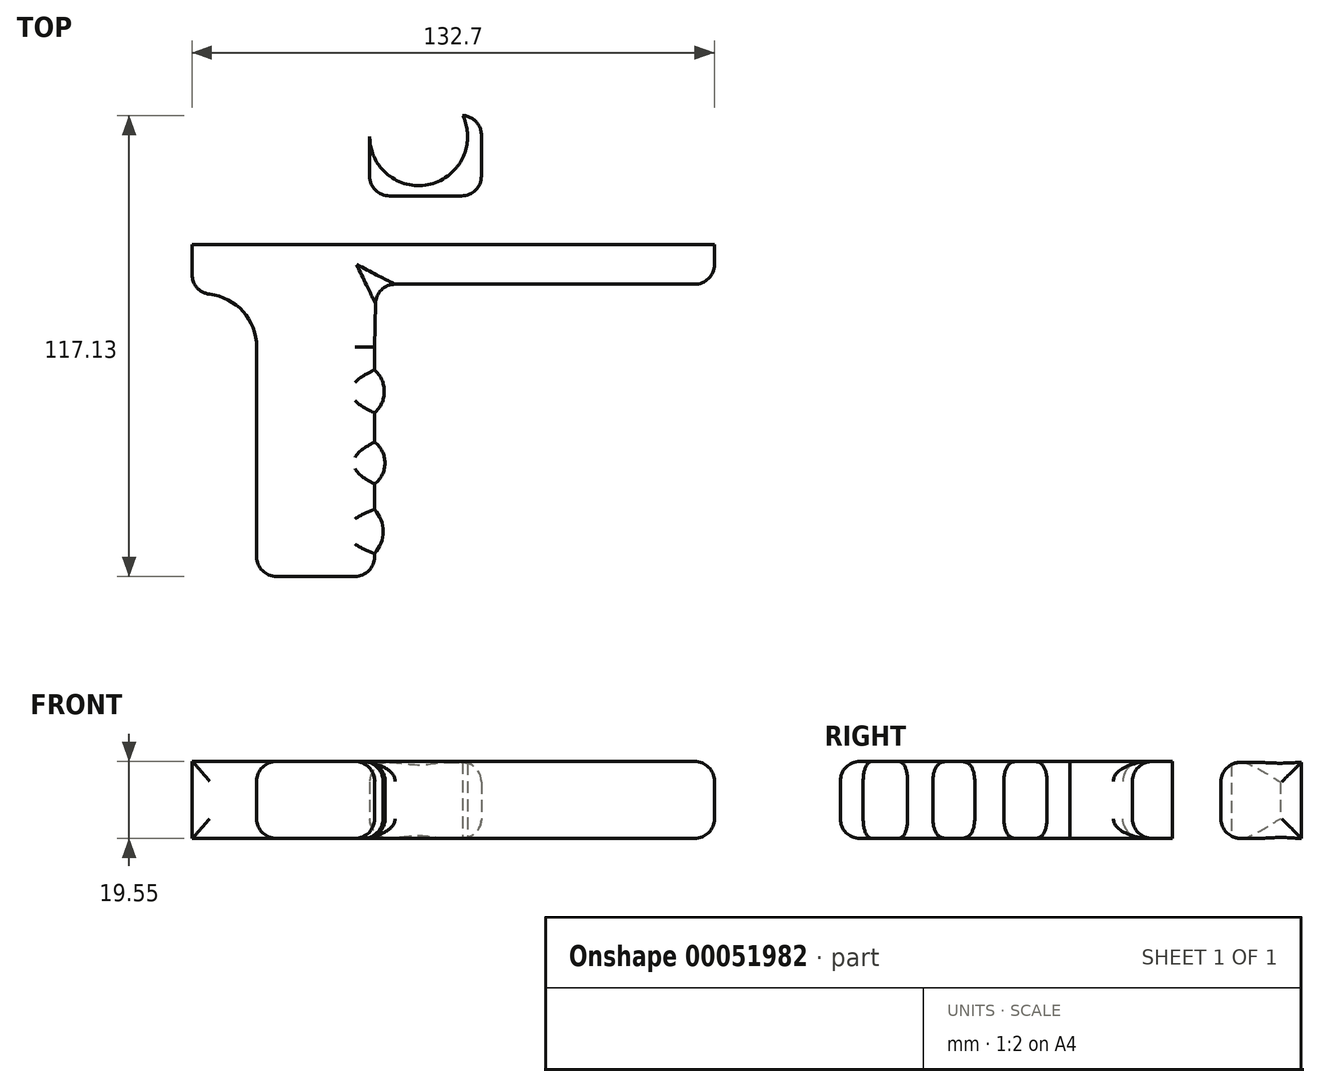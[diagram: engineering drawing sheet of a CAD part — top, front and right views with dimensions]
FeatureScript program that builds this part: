
annotation { "Feature Type Name" : "Feature", "Feature Type Description" : "" }
export const myFeature = defineFeature(function(context is Context, id is Id, definition is map)
    precondition{}
    {
        {
            var Q0;
            Q0=qCreatedBy(makeId("Top.planeOp"),FACE);
            var sketch = newSketch(context, id + "F0", { "sketchPlane" : qUnion([Q0])});
            skLineSegment(sketch, "E0.bottom", {"start": v(-44.45, -15.94) * mm, "end": v(-14.5, -15.94) * mm});
            skLineSegment(sketch, "E0.top", {"start": v(-44.45, -74.24) * mm, "end": v(-14.5, -74.24) * mm});
            skLineSegment(sketch, "E0.left", {"start": v(-44.45, -15.94) * mm, "end": v(-44.45, -74.24) * mm});
            skLineSegment(sketch, "E0.right", {"start": v(-14.5, -15.94) * mm, "end": v(-14.5, -74.24) * mm});
            skArc(sketch, "E1", {"start": v(-44.45, -15.94) * mm, "mid": v(-49.5, -5.4) * mm, "end": v(-60.87, -2.74) * mm});
            skLineSegment(sketch, "E2", {"start": v(-60.87, -2.74) * mm, "end": v(-60.87, 10.15) * mm});
            skLineSegment(sketch, "E3", {"start": v(-60.87, 10.15) * mm, "end": v(71.83, 10.15) * mm});
            skLineSegment(sketch, "E4", {"start": v(71.83, 10.15) * mm, "end": v(71.83, 0) * mm});
            skLineSegment(sketch, "E5", {"start": v(71.83, 0) * mm, "end": v(-6.76, 0) * mm});
            skLineSegment(sketch, "E6", {"start": v(-6.76, 0) * mm, "end": v(-14.17, 0) * mm});
            skLineSegment(sketch, "E7", {"start": v(-14.17, 0) * mm, "end": v(-14.5, -15.94) * mm});
            skArc(sketch, "E8", {"start": v(-14.5, -32.7) * mm, "mid": v(-12.02, -27.22) * mm, "end": v(-14.5, -21.74) * mm});
            skArc(sketch, "E9", {"start": v(-14.5, -50.73) * mm, "mid": v(-11.85, -45.41) * mm, "end": v(-14.5, -40.1) * mm});
            skArc(sketch, "E10", {"start": v(-14.5, -68.44) * mm, "mid": v(-12.36, -62.8) * mm, "end": v(-14.5, -57.17) * mm});
            skArc(sketch, "E11", {"start": v(-14.5, -15.94) * mm, "mid": v(6.33, -18.77) * mm, "end": v(15.78, 0) * mm});
            skArc(sketch, "E12", {"start": v(-6.76, 0) * mm, "mid": v(-7.48, -9.58) * mm, "end": v(0, -15.62) * mm});
            skArc(sketch, "E13", {"start": v(-4, 0) * mm, "mid": v(-4.47, -8.44) * mm, "end": v(0, -15.62) * mm});
            skSolve(sketch);
        }
        {
            var Q0;
            {var subQ0=sQuery(id+"F0.wireOp",EDGE,"E8");Q0=makeQuery(id+"F0.imprint","IMPRINT",FACE,{"disambiguationData":[TD([[makeQuery(id+"F0.imprint","IMPRINT",EDGE,{"derivedFrom":subQ0}),1.0]])]});}
            var Q1;
            {var subQ0=sQuery(id+"F0.wireOp",EDGE,"E9");Q1=makeQuery(id+"F0.imprint","IMPRINT",FACE,{"disambiguationData":[TD([[makeQuery(id+"F0.imprint","IMPRINT",EDGE,{"derivedFrom":subQ0}),1.0]])]});}
            var Q2;
            {var subQ0=sQuery(id+"F0.wireOp",EDGE,"E10");Q2=makeQuery(id+"F0.imprint","IMPRINT",FACE,{"disambiguationData":[TD([[makeQuery(id+"F0.imprint","IMPRINT",EDGE,{"derivedFrom":subQ0}),1.0]])]});}
            var Q3;
            Q3=makeQuery(id+"F0.imprint","IMPRINT",FACE,{"disambiguationData":[TD([[makeQuery(id+"F0.imprint","IMPRINT",EDGE,{"derivedFrom":sQuery(id+"F0.wireOp",EDGE,"E0.bottom")}),1.0]])]});
            var Q4;
            {var subQ1=sQuery(id+"F0.wireOp",EDGE,"E0.bottom");Q4=makeQuery(id+"F0.imprint","IMPRINT",FACE,{"disambiguationData":[TD([[makeQuery(id+"F0.imprint","IMPRINT",EDGE,{"derivedFrom":subQ1}),-1.0]])]});}
            extrude(context, id + "F1", {"entities" : qUnion([Q0, Q1, Q2, Q3, Q4]), "depth" : 19.55 * mm});
        }
        {
            var Q0;
            Q0=makeQuery(id+"F1.opExtrude","SWEPT_EDGE",EDGE,{"disambiguationData":[OSD([sQuery(id+"F0.wireOp",EDGE,"E4"),sQuery(id+"F0.wireOp",EDGE,"E5")])]});
            var Q1;
            Q1=makeQuery(id+"F1.opExtrude","SWEPT_EDGE",EDGE,{"disambiguationData":[OSD([sQuery(id+"F0.wireOp",EDGE,"E1"),sQuery(id+"F0.wireOp",EDGE,"E2")])]});
            var Q2;
            Q2=makeQuery(id+"F1.opExtrude","SWEPT_EDGE",EDGE,{"disambiguationData":[OSD([sQuery(id+"F0.wireOp",EDGE,"E0.top"),sQuery(id+"F0.wireOp",EDGE,"E0.left")])]});
            var Q3;
            Q3=makeQuery(id+"F1.opExtrude","SWEPT_EDGE",EDGE,{"disambiguationData":[OSD([sQuery(id+"F0.wireOp",EDGE,"E0.top"),sQuery(id+"F0.wireOp",EDGE,"E0.right")])]});
            var Q4;
            Q4=makeQuery(id+"F1.opExtrude","CAP_EDGE",EDGE,{"disambiguationData":[OSD([sQuery(id+"F0.wireOp",EDGE,"E0.left")])],"isStart":false});
            var Q5;
            Q5=makeQuery(id+"F1.opExtrude","CAP_EDGE",EDGE,{"disambiguationData":[OSD([sQuery(id+"F0.wireOp",EDGE,"E0.left")])],"isStart":true});
            var Q6;
            Q6=makeQuery(id+"F1.opExtrude","CAP_EDGE",EDGE,{"disambiguationData":[OSD([sQuery(id+"F0.wireOp",EDGE,"E5"),sQuery(id+"F0.wireOp",EDGE,"E6")])],"isStart":false});
            var Q7;
            Q7=makeQuery(id+"F1.opExtrude","CAP_EDGE",EDGE,{"disambiguationData":[OSD([sQuery(id+"F0.wireOp",EDGE,"E5"),sQuery(id+"F0.wireOp",EDGE,"E6")])],"isStart":true});
            var Q8;
            Q8=makeQuery(id+"F1.opExtrude","CAP_EDGE",EDGE,{"disambiguationData":[OSD([sQuery(id+"F0.wireOp",EDGE,"E7")])],"isStart":false});
            var Q9;
            Q9=makeQuery(id+"F1.opExtrude","CAP_EDGE",EDGE,{"disambiguationData":[OSD([sQuery(id+"F0.wireOp",EDGE,"E7")])],"isStart":true});
            var Q10;
            {var subQ0=sQuery(id+"F0.wireOp",EDGE,"E0.right");Q10=makeQuery(id+"F1.opExtrude","CAP_EDGE",EDGE,{"disambiguationData":[OSD([subQ0]),TDD([makeQuery(id+"F0.imprint","IMPRINT",EDGE,{"disambiguationData":[TD([[makeQuery(id+"F0.imprint","INTERSECT",VERTEX,{"disambiguationData":[OD(0.0)],"derivedFrom":[subQ0,sQuery(id+"F0.wireOp",EDGE,"E8")]}),-1.0]])],"derivedFrom":subQ0})])],"isStart":false});}
            var Q11;
            {var subQ0=sQuery(id+"F0.wireOp",EDGE,"E0.right");Q11=makeQuery(id+"F1.opExtrude","CAP_EDGE",EDGE,{"disambiguationData":[OSD([subQ0]),TDD([makeQuery(id+"F0.imprint","IMPRINT",EDGE,{"disambiguationData":[TD([[makeQuery(id+"F0.imprint","INTERSECT",VERTEX,{"disambiguationData":[OD(0.0)],"derivedFrom":[subQ0,sQuery(id+"F0.wireOp",EDGE,"E8")]}),-1.0]])],"derivedFrom":subQ0})])],"isStart":true});}
            var Q12;
            {var subQ0=sQuery(id+"F0.wireOp",EDGE,"E0.right");Q12=makeQuery(id+"F1.opExtrude","CAP_EDGE",EDGE,{"disambiguationData":[OSD([subQ0]),TDD([makeQuery(id+"F0.imprint","IMPRINT",EDGE,{"disambiguationData":[TD([[makeQuery(id+"F0.imprint","INTERSECT",VERTEX,{"disambiguationData":[OD(0.0)],"derivedFrom":[subQ0,sQuery(id+"F0.wireOp",EDGE,"E9")]}),-1.0]])],"derivedFrom":subQ0})])],"isStart":true});}
            var Q13;
            {var subQ0=sQuery(id+"F0.wireOp",EDGE,"E0.right");Q13=makeQuery(id+"F1.opExtrude","CAP_EDGE",EDGE,{"disambiguationData":[OSD([subQ0]),TDD([makeQuery(id+"F0.imprint","IMPRINT",EDGE,{"disambiguationData":[TD([[makeQuery(id+"F0.imprint","INTERSECT",VERTEX,{"disambiguationData":[OD(0.0)],"derivedFrom":[subQ0,sQuery(id+"F0.wireOp",EDGE,"E9")]}),-1.0]])],"derivedFrom":subQ0})])],"isStart":false});}
            var Q14;
            {var subQ0=sQuery(id+"F0.wireOp",EDGE,"E0.right");Q14=makeQuery(id+"F1.opExtrude","CAP_EDGE",EDGE,{"disambiguationData":[OSD([subQ0]),TDD([makeQuery(id+"F0.imprint","IMPRINT",EDGE,{"disambiguationData":[TD([[makeQuery(id+"F0.imprint","INTERSECT",VERTEX,{"derivedFrom":[sQuery(id+"F0.wireOp",EDGE,"E0.top"),subQ0]}),1.0]])],"derivedFrom":subQ0})])],"isStart":false});}
            var Q15;
            {var subQ0=sQuery(id+"F0.wireOp",EDGE,"E0.right");Q15=makeQuery(id+"F1.opExtrude","CAP_EDGE",EDGE,{"disambiguationData":[OSD([subQ0]),TDD([makeQuery(id+"F0.imprint","IMPRINT",EDGE,{"disambiguationData":[TD([[makeQuery(id+"F0.imprint","INTERSECT",VERTEX,{"derivedFrom":[sQuery(id+"F0.wireOp",EDGE,"E0.top"),subQ0]}),1.0]])],"derivedFrom":subQ0})])],"isStart":true});}
            var Q16;
            Q16=makeQuery(id+"F1.opExtrude","CAP_EDGE",EDGE,{"disambiguationData":[OSD([sQuery(id+"F0.wireOp",EDGE,"E4")])],"isStart":true});
            var Q17;
            Q17=makeQuery(id+"F1.opExtrude","CAP_EDGE",EDGE,{"disambiguationData":[OSD([sQuery(id+"F0.wireOp",EDGE,"E4")])],"isStart":false});
            fillet(context, id + "F2", {"entities" : qUnion([Q0, Q1, Q2, Q3, Q4, Q5, Q6, Q7, Q8, Q9, Q10, Q11, Q12, Q13, Q14, Q15, Q16, Q17]), "radius" : 5 * mm, "tangentPropagation" : true, "allowEdgeOverflow" : false});
        }
        {
            var Q0;
            Q0=makeQuery(id+"F1.opExtrude","CAP_EDGE",EDGE,{"disambiguationData":[OSD([sQuery(id+"F0.wireOp",EDGE,"E8")])],"isStart":false});
            var Q1;
            Q1=makeQuery(id+"F1.opExtrude","CAP_EDGE",EDGE,{"disambiguationData":[OSD([sQuery(id+"F0.wireOp",EDGE,"E8")])],"isStart":true});
            var Q2;
            Q2=makeQuery(id+"F1.opExtrude","CAP_EDGE",EDGE,{"disambiguationData":[OSD([sQuery(id+"F0.wireOp",EDGE,"E9")])],"isStart":false});
            var Q3;
            Q3=makeQuery(id+"F1.opExtrude","CAP_EDGE",EDGE,{"disambiguationData":[OSD([sQuery(id+"F0.wireOp",EDGE,"E10")])],"isStart":false});
            var Q4;
            Q4=makeQuery(id+"F1.opExtrude","CAP_EDGE",EDGE,{"disambiguationData":[OSD([sQuery(id+"F0.wireOp",EDGE,"E9")])],"isStart":true});
            var Q5;
            Q5=makeQuery(id+"F1.opExtrude","CAP_EDGE",EDGE,{"disambiguationData":[OSD([sQuery(id+"F0.wireOp",EDGE,"E10")])],"isStart":true});
            fillet(context, id + "F3", {"entities" : qUnion([Q0, Q1, Q2, Q3, Q4, Q5]), "radius" : 5 * mm, "tangentPropagation" : true, "allowEdgeOverflow" : false});
        }
        {
            var Q0;
            Q0=makeQuery(id+"F1.opExtrude","CAP_EDGE",EDGE,{"disambiguationData":[OSD([sQuery(id+"F0.wireOp",EDGE,"E0.top")])],"isStart":false});
            var Q1;
            Q1=makeQuery(id+"F1.opExtrude","CAP_EDGE",EDGE,{"disambiguationData":[OSD([sQuery(id+"F0.wireOp",EDGE,"E0.top")])],"isStart":true});
            fillet(context, id + "F4", {"entities" : qUnion([Q0, Q1]), "radius" : 5 * mm, "tangentPropagation" : true, "allowEdgeOverflow" : false});
        }
        {
            var Q0;
            Q0=makeQuery(id+"F1.opExtrude","SWEPT_EDGE",EDGE,{"disambiguationData":[OSD([sQuery(id+"F0.wireOp",EDGE,"E6"),sQuery(id+"F0.wireOp",EDGE,"E7")])]});
            fillet(context, id + "F5", {"entities" : qUnion([Q0]), "radius" : 5 * mm, "tangentPropagation" : true, "allowEdgeOverflow" : false});
        }
        {
            var Q0;
            Q0=qCreatedBy(makeId("Top.planeOp"),FACE);
            var sketch = newSketch(context, id + "F6", { "sketchPlane" : qUnion([Q0])});
            skLineSegment(sketch, "E14", {"start": v(-15.74, 37.51) * mm, "end": v(-15.74, 22.47) * mm});
            skArc(sketch, "E15", {"start": v(-15.74, 37.51) * mm, "mid": v(-0.55, 25.39) * mm, "end": v(7.9, 42.89) * mm});
            skLineSegment(sketch, "E16", {"start": v(-15.74, 22.47) * mm, "end": v(12.64, 22.47) * mm});
            skLineSegment(sketch, "E17", {"start": v(12.64, 22.47) * mm, "end": v(12.64, 42.89) * mm});
            skLineSegment(sketch, "E18", {"start": v(7.9, 42.89) * mm, "end": v(12.64, 42.89) * mm});
            skSolve(sketch);
        }
        {
            var Q0;
            Q0=makeQuery(id+"F6.imprint","IMPRINT",FACE,{"disambiguationData":[TD([[makeQuery(id+"F6.imprint","IMPRINT",EDGE,{"derivedFrom":sQuery(id+"F6.wireOp",EDGE,"E14")}),1.0]])]});
            extrude(context, id + "F7", {"entities" : qUnion([Q0]), "depth" : 19.34 * mm});
        }
        {
            var Q0;
            Q0=makeQuery(id+"F7.opExtrude","SWEPT_EDGE",EDGE,{"disambiguationData":[OSD([sQuery(id+"F6.wireOp",EDGE,"E16"),sQuery(id+"F6.wireOp",EDGE,"E17")])]});
            var Q1;
            Q1=makeQuery(id+"F7.opExtrude","SWEPT_EDGE",EDGE,{"disambiguationData":[OSD([sQuery(id+"F6.wireOp",EDGE,"E14"),sQuery(id+"F6.wireOp",EDGE,"E16")])]});
            var Q2;
            Q2=makeQuery(id+"F7.opExtrude","CAP_EDGE",EDGE,{"disambiguationData":[OSD([sQuery(id+"F6.wireOp",EDGE,"E16")])],"isStart":false});
            var Q3;
            Q3=makeQuery(id+"F7.opExtrude","CAP_EDGE",EDGE,{"disambiguationData":[OSD([sQuery(id+"F6.wireOp",EDGE,"E16")])],"isStart":true});
            var Q4;
            Q4=makeQuery(id+"F7.opExtrude","CAP_EDGE",EDGE,{"disambiguationData":[OSD([sQuery(id+"F6.wireOp",EDGE,"E17")])],"isStart":true});
            var Q5;
            Q5=makeQuery(id+"F7.opExtrude","CAP_EDGE",EDGE,{"disambiguationData":[OSD([sQuery(id+"F6.wireOp",EDGE,"E14")])],"isStart":true});
            var Q6;
            Q6=makeQuery(id+"F7.opExtrude","CAP_EDGE",EDGE,{"disambiguationData":[OSD([sQuery(id+"F6.wireOp",EDGE,"E17")])],"isStart":false});
            var Q7;
            Q7=makeQuery(id+"F7.opExtrude","CAP_EDGE",EDGE,{"disambiguationData":[OSD([sQuery(id+"F6.wireOp",EDGE,"E14")])],"isStart":false});
            var Q8;
            Q8=makeQuery(id+"F7.opExtrude","SWEPT_EDGE",EDGE,{"disambiguationData":[OSD([sQuery(id+"F6.wireOp",EDGE,"E17"),sQuery(id+"F6.wireOp",EDGE,"E18")])]});
            fillet(context, id + "F8", {"entities" : qUnion([Q0, Q1, Q2, Q3, Q4, Q5, Q6, Q7, Q8]), "radius" : 5 * mm, "tangentPropagation" : true, "allowEdgeOverflow" : false});
        }
    });
